# Revit family: revitupgrade
name_source: partatom
category: Furniture
units: mm (PartAtom-declared; Revit-internal decimal feet)

## family parameters
Always vertical = Yes
Cut with Voids When Loaded = No
Enable Cutting in Views = No
OmniClass Number = 23.40.70.14.64.11
OmniClass Title = Office Furniture
Render Appearance Source = Family Geometry
Room Calculation Point = No
Shared = No
Work Plane-Based = No

## types (2) — shared parameters
Assembly Code = E2020200
Default Elevation = 0.00 mm
Description = A collection of highback sofas that breathe a sense of calmness, concentration and comfort into everyday life in the workplace and in hospitality contexts.
Manufacturer = Wendelbo
Release Date = January 2022
Style Number(s) = WBOCASEMT
Table Finish = Wedelbo - Metal - Black Powder Coated
URL = https://www.steelcase.com

## per-type parameters (varying)
| type | Left Side | Right Side |
| Right Side Table | No | Yes |
| Left Side Table | Yes | No |

## geometry (parser evidence)
native form markers: Sweep x4
no freeform markers — native parametric forms only
